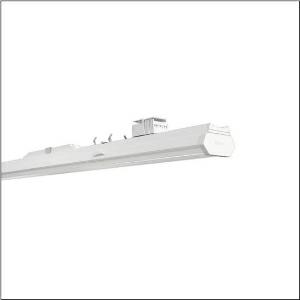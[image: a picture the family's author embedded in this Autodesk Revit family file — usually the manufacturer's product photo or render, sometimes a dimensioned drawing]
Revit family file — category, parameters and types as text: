
# Revit family: licross_r__11_protected_ho_51td13mn4gxs_7737
name_source: partatom
category: Lighting Fixtures
units: mm (PartAtom-declared; Revit-internal decimal feet)

## family parameters
Cut with Voids When Loaded = No
Host = Face
Light Source = No
Part Type = Normal
Room Calculation Point = No
Round Connector Dimension = Use Diameter
Shared = No

## types (1)
- --- (1 x LED, 16110 lm, 87.4 W, 4000K)
    Apparent Load = 87 VA
    CIE Flux Codes = 89 96 99 100 99
    Color Rendering = 80
    Color Temperature = 4000K
    Default Elevation = 1800 mm
    Description = Licross® 11 Protected HO, luminaire insert, of sheet steel, galvanised, coil coated, white, length: 1.500mm, width: 90mm, height: 101mm, LED rated luminous flux: 16.110lm, light colour: 840, control gear: ON/OFF Multilumen, with plug, 3-pole, with phase selection, mains connection: 220..240V, AC, 50/60Hz, rated input power: 87W, internal wiring halogen-free, primary light control with lens, of plastic, primary optical cover: cover, of PMMA, light emission: direct distribution, primary light characteristic: symmetric, protection rating (complete): IP54, insulation class (complete): insulation class I (protective earthing), certification: CE, ENEC, VDE, UKCA, protection symbol: D if used in an environment with non-conductive dust loads with corresponding accessories, impact resistance: IK06, permissible ambient temperature for indoor applications: -35..+35°C, corresponds to IFS (International Featured Standards) requirements for safety and quality in the food industry, reducing of maximum allowable ambient temperature of 5°C with ceiling mounting, LABS conformity tested according to VDMA 24364:2018-05, packaging unit: 1 piece
    Height = 92 mm
    Lamp = 1 x LED
    Lamp Light Flux = 16110 lm
    Lamp Power = 87.4 W
    Lamp count = 1
    Length = 1500 mm
    Luminous efficacy = 184 lm/W
    Manufacturer = Siteco
    ModVariant = No
    Model = 51TD13MN4GXS
    Mounting Place = Ceiling
    Mounting Type = Pendant
    Number of Poles = 1
    OnlyDefault = Yes
    Power Factor = 1
    Product Name = Licross® 11 Protected HO
    Product group = luminaire insert | ceiling pendant
    ProductGroupID = 902
    Protection Class = Protection class I
    Protection Degree = IP 54
    RLX_Detail_Level = 1
    RLX_Emergency_Light_Flux = 0 lm
    RLX_Emergency_Type = 0
    RLX_Emergency_Type_DB = No
    RlxData = <blob elided: 21965 chars, md5=166324e5>
    Socket = socket
    Standby Power = 0 W
    System Light Flux = 16110 lm
    System Power = 87 W
    Type Comments = factory setting: luminous flux: 100 % | (A | C | E) | 203 mA
    Type Image = l_1256145.jpg
    URL = http://relux.com
    VarID = @adj_107241
    Voltage = 0 V
    Weight = 0.00 kg
    Width = 88 mm

## geometry (parser evidence)
native form markers: Blend x4, Sweep x11
no freeform markers — native parametric forms only
